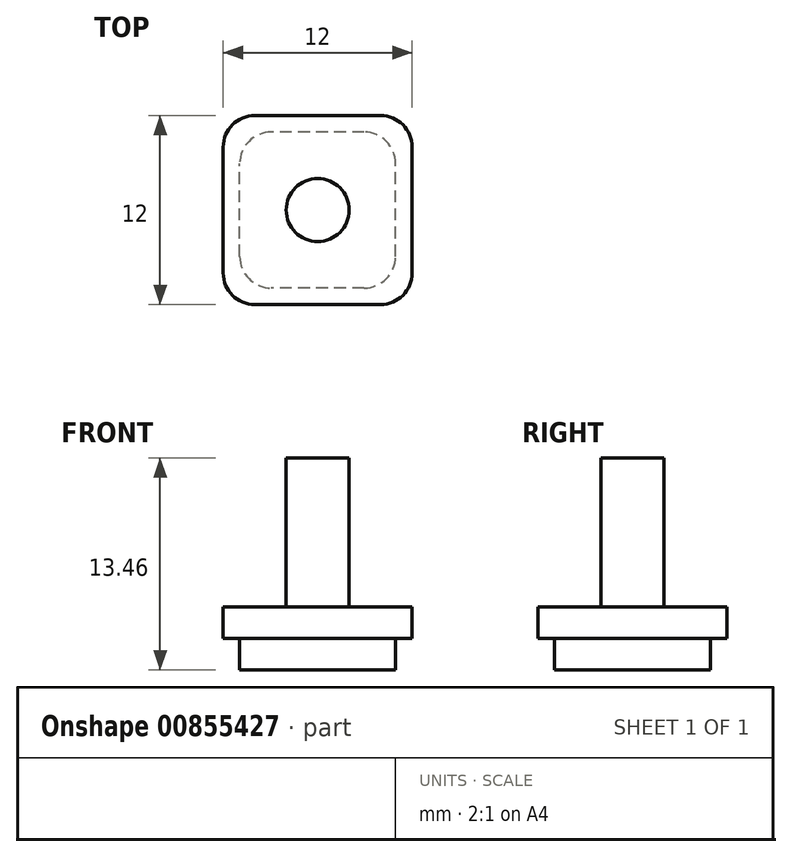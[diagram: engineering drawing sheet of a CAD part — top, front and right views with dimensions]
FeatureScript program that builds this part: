
annotation { "Feature Type Name" : "Feature", "Feature Type Description" : "" }
export const myFeature = defineFeature(function(context is Context, id is Id, definition is map)
    precondition{}
    {
        {
            var Q0;
            Q0=qCreatedBy(makeId("Top.planeOp"),FACE);
            var sketch = newSketch(context, id + "F0", { "sketchPlane" : qUnion([Q0])});
            skLineSegment(sketch, "E0.bottom", {"start": v(2.95, -4.95) * mm, "end": v(-2.95, -4.95) * mm});
            skLineSegment(sketch, "E0.top", {"start": v(2.95, 4.95) * mm, "end": v(-2.95, 4.95) * mm});
            skLineSegment(sketch, "E0.left", {"start": v(4.95, -2.95) * mm, "end": v(4.95, 2.95) * mm});
            skLineSegment(sketch, "E0.right", {"start": v(-4.95, -2.95) * mm, "end": v(-4.95, 2.95) * mm});
            skPoint(sketch, "E0.middle", {"position": v(0, 0) * mm});
            skPoint(sketch, "E1.visualSharp", {"position": v(-4.95, 4.95) * mm});
            skArc(sketch, "E1.filletArc", {"start": v(-2.95, 4.95) * mm, "mid": v(-4.36, 4.36) * mm, "end": v(-4.95, 2.95) * mm});
            skPoint(sketch, "E2.visualSharp", {"position": v(4.95, 4.95) * mm});
            skArc(sketch, "E2.filletArc", {"start": v(4.95, 2.95) * mm, "mid": v(4.36, 4.36) * mm, "end": v(2.95, 4.95) * mm});
            skPoint(sketch, "E3.visualSharp", {"position": v(4.95, -4.95) * mm});
            skArc(sketch, "E3.filletArc", {"start": v(2.95, -4.95) * mm, "mid": v(4.36, -4.36) * mm, "end": v(4.95, -2.95) * mm});
            skPoint(sketch, "E4.visualSharp", {"position": v(-4.95, -4.95) * mm});
            skArc(sketch, "E4.filletArc", {"start": v(-4.95, -2.95) * mm, "mid": v(-4.36, -4.36) * mm, "end": v(-2.95, -4.95) * mm});
            skSolve(sketch);
        }
        {
            var Q0;
            Q0 = qSketchRegion(id + "F0", true);
            extrude(context, id + "F1", {"entities" : qUnion([Q0]), "depth" : 2 * mm, "offsetDistance" : 25 * mm});
        }
        {
            var Q0;
            Q0=makeQuery(id+"F1.opExtrude","CAP_FACE",FACE,{"disambiguationData":[OSD([sQuery(id+"F0.wireOp",EDGE,"E0.bottom"),sQuery(id+"F0.wireOp",EDGE,"E0.top"),sQuery(id+"F0.wireOp",EDGE,"E0.left"),sQuery(id+"F0.wireOp",EDGE,"E0.right"),sQuery(id+"F0.wireOp",EDGE,"E1.filletArc"),sQuery(id+"F0.wireOp",EDGE,"E2.filletArc"),sQuery(id+"F0.wireOp",EDGE,"E3.filletArc"),sQuery(id+"F0.wireOp",EDGE,"E4.filletArc")])],"isStart":false});
            var sketch = newSketch(context, id + "F2", { "sketchPlane" : qUnion([Q0])});
            skLineSegment(sketch, "E5.bottom", {"start": v(4, -6) * mm, "end": v(-4, -6) * mm});
            skLineSegment(sketch, "E5.top", {"start": v(4, 6) * mm, "end": v(-4, 6) * mm});
            skLineSegment(sketch, "E5.left", {"start": v(6, -4) * mm, "end": v(6, 4) * mm});
            skLineSegment(sketch, "E5.right", {"start": v(-6, -4) * mm, "end": v(-6, 4) * mm});
            skPoint(sketch, "E5.middle", {"position": v(0, 0) * mm});
            skPoint(sketch, "E6.visualSharp", {"position": v(-6, 6) * mm});
            skArc(sketch, "E6.filletArc", {"start": v(-4, 6) * mm, "mid": v(-5.41, 5.41) * mm, "end": v(-6, 4) * mm});
            skPoint(sketch, "E7.visualSharp", {"position": v(6, 6) * mm});
            skArc(sketch, "E7.filletArc", {"start": v(6, 4) * mm, "mid": v(5.41, 5.41) * mm, "end": v(4, 6) * mm});
            skPoint(sketch, "E8.visualSharp", {"position": v(6, -6) * mm});
            skArc(sketch, "E8.filletArc", {"start": v(4, -6) * mm, "mid": v(5.41, -5.41) * mm, "end": v(6, -4) * mm});
            skPoint(sketch, "E9.visualSharp", {"position": v(-6, -6) * mm});
            skArc(sketch, "E9.filletArc", {"start": v(-6, -4) * mm, "mid": v(-5.41, -5.41) * mm, "end": v(-4, -6) * mm});
            skSolve(sketch);
        }
        {
            var Q0;
            Q0 = qSketchRegion(id + "F2", true);
            extrude(context, id + "F3", {"entities" : qUnion([Q0]), "operationType" : NewBodyOperationType.ADD, "depth" : 2 * mm, "offsetDistance" : 25 * mm});
        }
        {
            var Q0;
            Q0=makeQuery(id+"F3.opExtrude","CAP_FACE",FACE,{"disambiguationData":[OSD([sQuery(id+"F2.wireOp",EDGE,"E5.bottom"),sQuery(id+"F2.wireOp",EDGE,"E5.top"),sQuery(id+"F2.wireOp",EDGE,"E5.left"),sQuery(id+"F2.wireOp",EDGE,"E5.right"),sQuery(id+"F2.wireOp",EDGE,"E6.filletArc"),sQuery(id+"F2.wireOp",EDGE,"E7.filletArc"),sQuery(id+"F2.wireOp",EDGE,"E8.filletArc"),sQuery(id+"F2.wireOp",EDGE,"E9.filletArc")])],"isStart":false});
            var sketch = newSketch(context, id + "F4", { "sketchPlane" : qUnion([Q0])});
            skCircle(sketch, "E10", {"center": v(0, 0) * mm, "radius": 2 * mm});
            skSolve(sketch);
        }
        {
            var Q0;
            Q0 = qSketchRegion(id + "F4", true);
            extrude(context, id + "F5", {"entities" : qUnion([Q0]), "operationType" : NewBodyOperationType.ADD, "depth" : 9.46 * mm, "offsetDistance" : 25 * mm});
        }
    });
